# Revit family: Faucet-Two_Handle-American_Standard-Colony_Pro-7074_Series
name_source: partatom
category: Plumbing Fixtures
units: mm (PartAtom-declared; Revit-internal decimal feet)

## family parameters
Always vertical = No
Cut with Voids When Loaded = No
OmniClass Number = 23.45.55.17
OmniClass Title = Mixing Faucets
Part Type = Normal
Room Calculation Point = No
Round Connector Dimension = Use Diameter
Shared = Yes
Work Plane-Based = Yes

## types (2) — shared parameters
ADA Compliant = Yes
Assembly Code = D2020300
CEC Compliant = Yes
CW Connection = Yes
CWFU = 1.5
Cold Water Connection Diameter = 1/2"
Cold Water Connection Radius = 1/4"
Default Elevation = 0"
Eco-Cartridge 15Mm-Hot Or Cold M964005-0070A = No
Finish = Brass-American Standard-002-Polished Chrome
Flow Rate = 1.5 gpm/5.7 L/min
HW Connection = Yes
HWFU = 1.5
Height = 6 7/8"
Hot Water Connection Diameter = 1"
Hot Water Connection Radius = 1/4"
Installation Instruction Link = https://americanstandard.box.com
Installation Type = Deck Mounted
Length = 7 1/2"
Manufacturer = American Standard
Material = Brass-American Standard-002-Polished Chrome
Plastic Faucet Mounting Nuts 065800-0070A = No
Plug Button Visibility M964323-0070A = No
Price = Prices may vary. Please consult Manufacturer Representative for most up-to-date price list.
Product Documentation Link = https://americanstandard.box.com
Product Page URL = https://www.americanstandard-us.com
Revised Date = 02/20/2023
URL = http://www.americanstandard-us.com
Vent Connection = No
WFU = 2
Warranty Information = Limited Lifetime Warranty
Waste Connection = No
Width = 9 3/4"

## per-type parameters (varying)
| type | Aerator | Description | Hose End |
| 7074240.002 | No | Colony® PRO 2-Handle Laundry Faucet 1.5 gpm/5.7 L/min | Yes |
| 7074140.002 | Yes | Colony® PRO 2-Handle Bar Faucet 1.5 gpm/5.7 L/min | No |

note: column(s) folded — value = type name in every type: Model

## geometry (parser evidence)
native form markers: Sweep x2
no freeform markers — native parametric forms only
